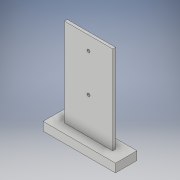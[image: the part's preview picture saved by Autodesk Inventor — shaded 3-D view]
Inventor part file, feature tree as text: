
AUTODESK INVENTOR PART (.ipt)
format: ipt  version: 2017 (Build 210142000, 142)  size: 130,048 bytes
history: native  units: in
note: dims shown in document units (in); Inventor stores cm internally (conversion verified against a paired STEP export)
features: extrude x2, sketch x2
ambient origin geometry x8: Origin, YZ Plane, XZ Plane, XY Plane, X Axis, Y Axis, Z Axis, Center Point
bodies: Solid1 (feature_tree)
feature tree (4):
  extrude  "Extrusion1"  Depth=0.1181in TaperAngle=0.0deg
  extrude  "Extrusion2"  Depth=3.0in TaperAngle=0.0deg
  sketch  "Sketch1"  dims[d0=1.575in d1=0.6in d2=2.4in d3=0.122in d4=0.122in d5=0.57in d6=1.0in d7=1.0in d8=4.0in d9=0.5in d10=0.5in d11=0.35in d12=0.1181in d13=0.0in]
  sketch  "Sketch2"  dims[d15=0.35in d17=3.0in d18=0.0in d19=0.3862in d20=0.386in]
